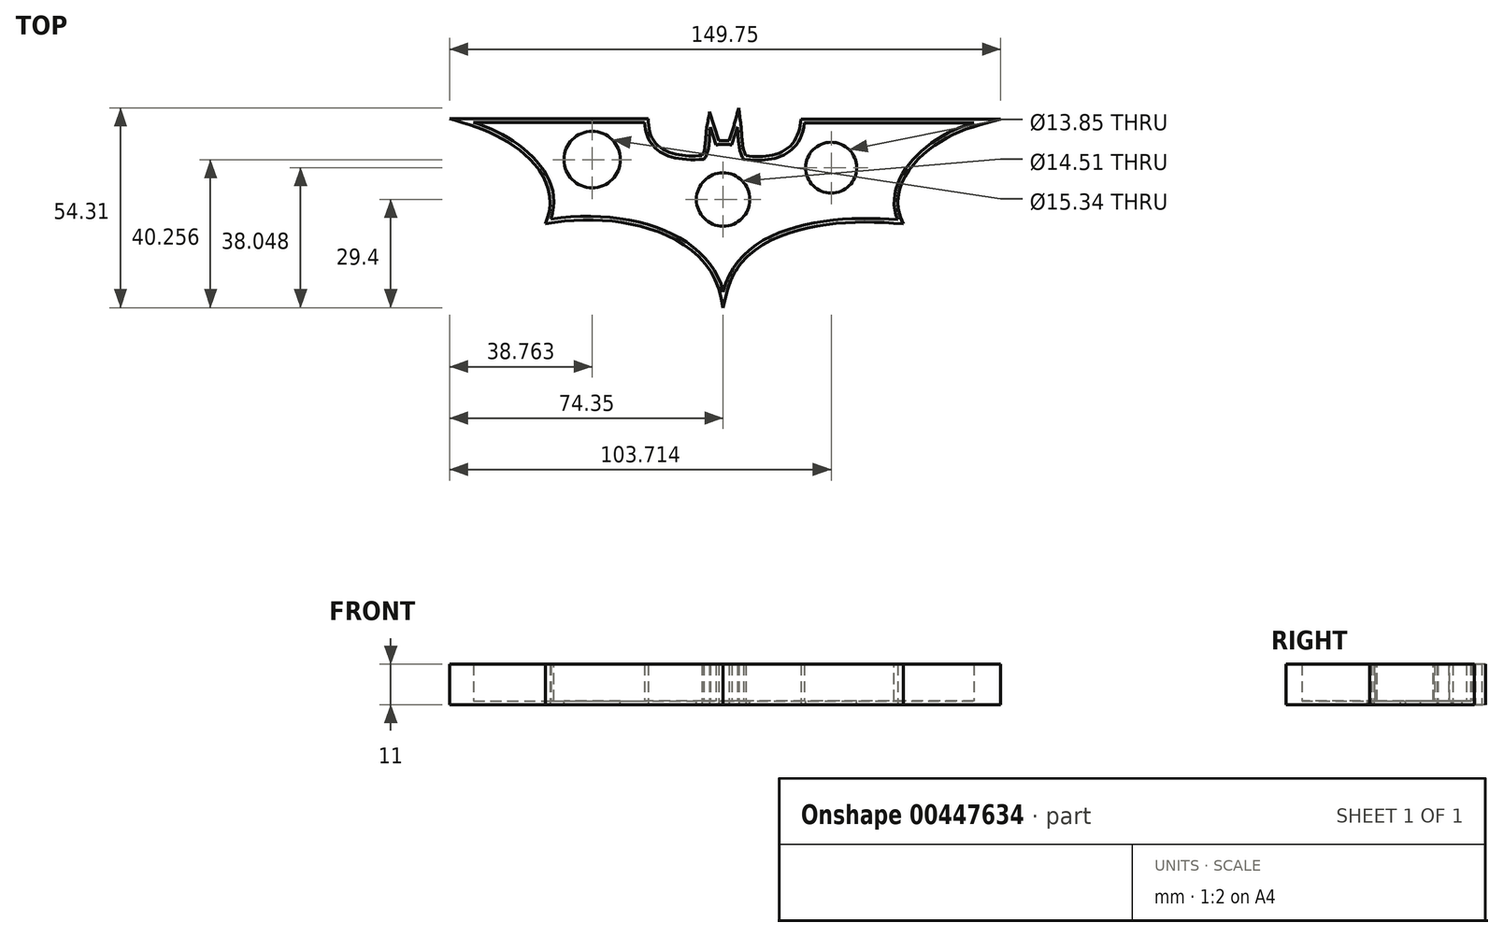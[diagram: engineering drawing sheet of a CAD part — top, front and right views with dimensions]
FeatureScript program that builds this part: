
annotation { "Feature Type Name" : "Feature", "Feature Type Description" : "" }
export const myFeature = defineFeature(function(context is Context, id is Id, definition is map)
    precondition{}
    {
        {
            var Q0;
            Q0=qCreatedBy(makeId("Top.planeOp"),FACE);
            var sketch = newSketch(context, id + "F0", { "sketchPlane" : qUnion([Q0])});
            skLineSegment(sketch, "E0", {"start": v(-67.86, 21.01) * mm, "end": v(-21.33, 21.01) * mm});
            skLineSegment(sketch, "E1", {"start": v(68.18, 20.87) * mm, "end": v(22.1, 20.87) * mm});
            skFitSpline(sketch, "E2", {"points": [v(-67.86, 21.01) * mm, v(-46.78, -5.31) * mm], "startDerivative": vector(36.6, -11.55) * mm, "endDerivative": vector(-12.47, -36.7) * mm});
            skFitSpline(sketch, "E3", {"points": [v(-46.78, -5.31) * mm, v(0, -25.08) * mm], "startDerivative": vector(61.4, 9.58) * mm, "endDerivative": vector(11.66, -48.67) * mm});
            skFitSpline(sketch, "E4", {"points": [v(0, -25.08) * mm, v(47.4, -5.51) * mm], "startDerivative": vector(13.02, 55.1) * mm, "endDerivative": vector(53.33, -4.74) * mm});
            skFitSpline(sketch, "E5", {"points": [v(47.4, -5.51) * mm, v(68.18, 20.87) * mm], "startDerivative": vector(-12.7, 31.66) * mm, "endDerivative": vector(42.01, 11.86) * mm});
            skFitSpline(sketch, "E6", {"points": [v(22.1, 20.87) * mm, v(5.59, 10.97) * mm], "startDerivative": vector(-3.8, -29.13) * mm, "endDerivative": vector(-21.84, 2.8) * mm});
            skFitSpline(sketch, "E7", {"points": [v(5.59, 10.97) * mm, v(3.86, 19.72) * mm], "startDerivative": vector(-4.66, 7.16) * mm, "endDerivative": vector(-1.02, 8.89) * mm});
            skFitSpline(sketch, "E8", {"points": [v(3.86, 19.72) * mm, v(2.34, 14.87) * mm], "startDerivative": vector(-1.36, -4.88) * mm, "endDerivative": vector(-1.36, -4.88) * mm});
            skFitSpline(sketch, "E9", {"points": [v(2.34, 14.87) * mm, v(-1.88, 14.87) * mm], "startDerivative": vector(-4.47, 0.6) * mm, "endDerivative": vector(-4.32, -0.68) * mm});
            skFitSpline(sketch, "E10", {"points": [v(-1.88, 14.87) * mm, v(-3.42, 19.72) * mm], "startDerivative": vector(-1.54, 4.85) * mm, "endDerivative": vector(-1.54, 4.85) * mm});
            skFitSpline(sketch, "E11", {"points": [v(-3.42, 19.72) * mm, v(-5.19, 10.97) * mm], "startDerivative": vector(-1.6, -8.63) * mm, "endDerivative": vector(-5.4, -7.27) * mm});
            skFitSpline(sketch, "E12", {"points": [v(-5.19, 10.97) * mm, v(-21.33, 21.01) * mm], "startDerivative": vector(-29.66, -2.34) * mm, "endDerivative": vector(-1.02, 23.43) * mm});
            skSolve(sketch);
        }
        {
            var Q0;
            Q0 = qSketchRegion(id + "F0", true);
            extrude(context, id + "F1", {"entities" : qUnion([Q0]), "depth" : 10 * mm});
        }
        {
            var Q0;
            Q0=makeQuery(id+"F1.opExtrude","CAP_FACE",FACE,{"disambiguationData":[OSD([sQuery(id+"F0.wireOp",EDGE,"E0"),sQuery(id+"F0.wireOp",EDGE,"E1"),sQuery(id+"F0.wireOp",EDGE,"E2"),sQuery(id+"F0.wireOp",EDGE,"E3"),sQuery(id+"F0.wireOp",EDGE,"E4"),sQuery(id+"F0.wireOp",EDGE,"E5"),sQuery(id+"F0.wireOp",EDGE,"E6"),sQuery(id+"F0.wireOp",EDGE,"E7"),sQuery(id+"F0.wireOp",EDGE,"E8"),sQuery(id+"F0.wireOp",EDGE,"E9"),sQuery(id+"F0.wireOp",EDGE,"E10"),sQuery(id+"F0.wireOp",EDGE,"E11"),sQuery(id+"F0.wireOp",EDGE,"E12")])],"isStart":false});
            shell(context, id + "F2", {"entities" : qUnion([Q0]), "thickness" : 1 * mm, "oppositeDirection" : true});
        }
        {
            var Q0;
            Q0=makeQuery(id+"F2.opShell","OFFSET_FACE",FACE,{"disambiguationData":[OSD([sQuery(id+"F0.wireOp",EDGE,"E0"),sQuery(id+"F0.wireOp",EDGE,"E1"),sQuery(id+"F0.wireOp",EDGE,"E2"),sQuery(id+"F0.wireOp",EDGE,"E3"),sQuery(id+"F0.wireOp",EDGE,"E4"),sQuery(id+"F0.wireOp",EDGE,"E5"),sQuery(id+"F0.wireOp",EDGE,"E6"),sQuery(id+"F0.wireOp",EDGE,"E7"),sQuery(id+"F0.wireOp",EDGE,"E8"),sQuery(id+"F0.wireOp",EDGE,"E9"),sQuery(id+"F0.wireOp",EDGE,"E10"),sQuery(id+"F0.wireOp",EDGE,"E11"),sQuery(id+"F0.wireOp",EDGE,"E12")])]});
            var sketch = newSketch(context, id + "F3", { "sketchPlane" : qUnion([Q0])});
            skCircle(sketch, "E13", {"center": v(-35.59, 10.86) * mm, "radius": 7.67 * mm});
            skCircle(sketch, "E14", {"center": v(0, 0) * mm, "radius": 7.26 * mm});
            skCircle(sketch, "E15", {"center": v(29.36, 8.65) * mm, "radius": 6.93 * mm});
            skSolve(sketch);
        }
        {
            var Q0;
            Q0=makeQuery(id+"F3.imprint","IMPRINT",FACE,{"disambiguationData":[TD([[makeQuery(id+"F3.imprint","IMPRINT",EDGE,{"derivedFrom":sQuery(id+"F3.wireOp",EDGE,"E13")}),1.0]])]});
            var Q1;
            Q1=makeQuery(id+"F3.imprint","IMPRINT",FACE,{"disambiguationData":[TD([[makeQuery(id+"F3.imprint","IMPRINT",EDGE,{"derivedFrom":sQuery(id+"F3.wireOp",EDGE,"E14")}),1.0]])]});
            var Q2;
            Q2=makeQuery(id+"F3.imprint","IMPRINT",FACE,{"disambiguationData":[TD([[makeQuery(id+"F3.imprint","IMPRINT",EDGE,{"derivedFrom":sQuery(id+"F3.wireOp",EDGE,"E15")}),1.0]])]});
            extrude(context, id + "F4", {"entities" : qUnion([Q0, Q1, Q2]), "operationType" : NewBodyOperationType.REMOVE, "oppositeDirection" : true, "depth" : 25 * mm});
        }
    });
